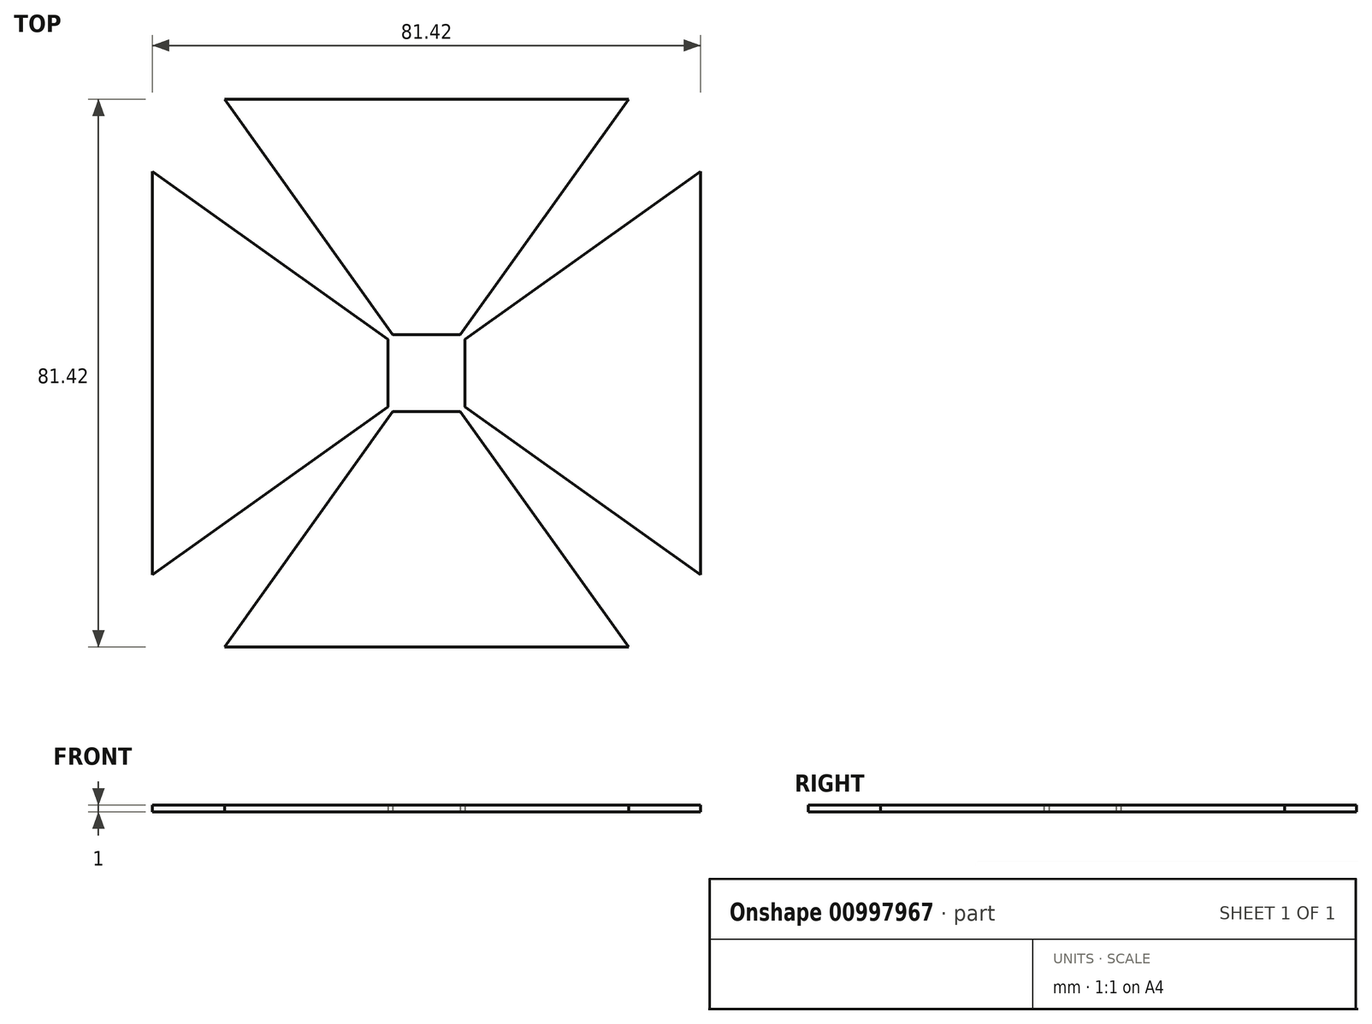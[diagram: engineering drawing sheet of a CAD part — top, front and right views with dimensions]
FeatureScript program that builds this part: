
annotation { "Feature Type Name" : "Feature", "Feature Type Description" : "" }
export const myFeature = defineFeature(function(context is Context, id is Id, definition is map)
    precondition{}
    {
        {
            var Q0;
            Q0=qCreatedBy(makeId("Top.planeOp"),FACE);
            var sketch = newSketch(context, id + "F0", { "sketchPlane" : qUnion([Q0])});
            skLineSegment(sketch, "E0", {"start": v(-30, 40.7) * mm, "end": v(30, 40.7) * mm});
            skLineSegment(sketch, "E1", {"start": v(30, 40.7) * mm, "end": v(5, 5.7) * mm});
            skLineSegment(sketch, "E2", {"start": v(5, 5.7) * mm, "end": v(-5, 5.7) * mm});
            skLineSegment(sketch, "E3", {"start": v(-5, 5.7) * mm, "end": v(-30, 40.7) * mm});
            skLineSegment(sketch, "E4.1.0", {"start": v(-40.7, -30) * mm, "end": v(-40.7, 30) * mm});
            skLineSegment(sketch, "E4.1.1", {"start": v(-5.7, -5) * mm, "end": v(-40.7, -30) * mm});
            skLineSegment(sketch, "E4.1.2", {"start": v(-40.7, 30) * mm, "end": v(-5.7, 5) * mm});
            skLineSegment(sketch, "E4.1.3", {"start": v(-5.7, 5) * mm, "end": v(-5.7, -5) * mm});
            skLineSegment(sketch, "E4.2.0", {"start": v(30, -40.7) * mm, "end": v(-30, -40.7) * mm});
            skLineSegment(sketch, "E4.2.1", {"start": v(5, -5.7) * mm, "end": v(30, -40.7) * mm});
            skLineSegment(sketch, "E4.2.2", {"start": v(-30, -40.7) * mm, "end": v(-5, -5.7) * mm});
            skLineSegment(sketch, "E4.2.3", {"start": v(-5, -5.7) * mm, "end": v(5, -5.7) * mm});
            skLineSegment(sketch, "E4.3.0", {"start": v(40.7, 30) * mm, "end": v(40.7, -30) * mm});
            skLineSegment(sketch, "E4.3.1", {"start": v(5.7, 5) * mm, "end": v(40.7, 30) * mm});
            skLineSegment(sketch, "E4.3.2", {"start": v(40.7, -30) * mm, "end": v(5.7, -5) * mm});
            skLineSegment(sketch, "E4.3.3", {"start": v(5.7, -5) * mm, "end": v(5.7, 5) * mm});
            skPoint(sketch, "E4.center", {"position": v(0, 0) * mm});
            skSolve(sketch);
        }
        {
            var Q0;
            Q0 = qSketchRegion(id + "F0", true);
            extrude(context, id + "F1", {"entities" : qUnion([Q0]), "flatOperationType" : FlatOperationType.REMOVE, "depth" : 1 * mm, "offsetDistance" : 25 * mm, "domain" : OperationDomain.MODEL});
        }
    });
